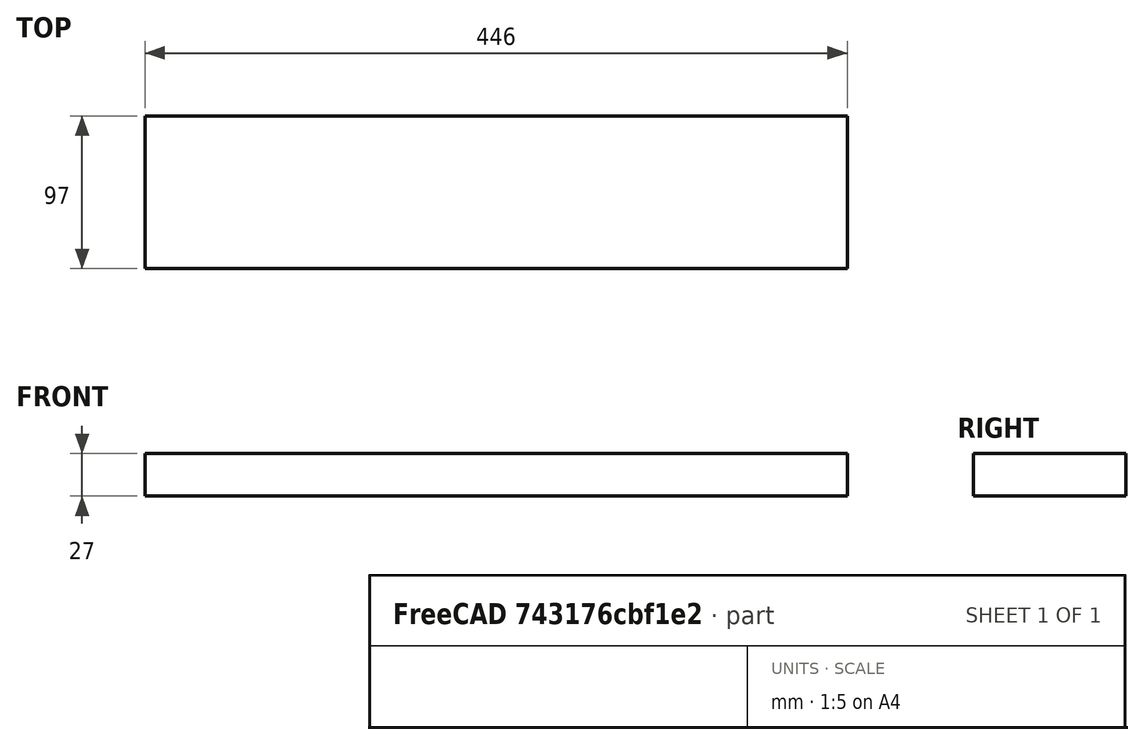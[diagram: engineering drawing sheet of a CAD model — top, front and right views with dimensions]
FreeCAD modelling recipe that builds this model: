
FCSTD DOCUMENT  (FreeCAD 0.20R25131 (Git))
Label: Innen_hinten
License: All rights reserved
LicenseURL: http://en.wikipedia.org/wiki/All_rights_reserved
objects: Part::FeaturePython×8, App::FeaturePython×2, Part::Box×1
note: 8 computed .brp shape members not serialized (recipe doc carries the construction recipe); baked Part::Feature solids carry a one-line shape summary decoded from their .brp
EXTERNAL_REF file=Grunddaten.FCStd obj=Spreadsheet

FEATURE [Part::Box] Box  label="Cube"
  AttacherType = Attacher::AttachEngine3D
  Height = 27
  Length = 446
  Width = 97
  expr: Length = <<Grunddaten>>#Spreadsheet.Innenmass
  expr: Width = <<Grunddaten>>#Spreadsheet.Hoehe
  expr: Height = <<Grunddaten>>#Spreadsheet.Plattendicke
FEATURE [App::FeaturePython] Constraints  # WARN: FeaturePython — macro-defined, semantics opaque (R4)
  _Version = 1
FEATURE [Part::FeaturePython] Parts  # WARN: FeaturePython — macro-defined, semantics opaque (R4)
  Group = -> [Box]
  GroupMode = 0
FEATURE [Part::FeaturePython] Assembly  label="Innen_hinten"  # WARN: FeaturePython — macro-defined, semantics opaque (R4)
  AutoRelax = true
  BuildShape = 0
  Freeze = false
  Group = -> [Constraints,Elements,Parts]
  Verbose = false
  _SolverType = 1
  _Version = 1
FEATURE [App::FeaturePython] Elements  # WARN: FeaturePython — macro-defined, semantics opaque (R4)
  Group = -> [Element,Element001,Element002,Element003,Element004,Element005]
FEATURE [Part::FeaturePython] Element  label="Oben"  # link proxy (typed FeaturePython)
  Detach = false
  LinkTransform = true
  LinkedObject = -> Box [Face4]
  _Parent = -> Elements
FEATURE [Part::FeaturePython] Element001  label="Hinten"  # link proxy (typed FeaturePython)
  Detach = false
  LinkTransform = true
  LinkedObject = -> Box [Face5]
  _Parent = -> Elements
FEATURE [Part::FeaturePython] Element002  # link proxy (typed FeaturePython)
  Detach = false
  LinkTransform = true
  LinkedObject = -> Box [Face1]
  _Parent = -> Elements
FEATURE [Part::FeaturePython] Element003  # link proxy (typed FeaturePython)
  Detach = false
  LinkTransform = true
  LinkedObject = -> Box [Face6]
  _Parent = -> Elements
FEATURE [Part::FeaturePython] Element004  # link proxy (typed FeaturePython)
  Detach = false
  LinkTransform = true
  LinkedObject = -> Box [Face2]
  _Parent = -> Elements
FEATURE [Part::FeaturePython] Element005  # link proxy (typed FeaturePython)
  Detach = false
  LinkTransform = true
  LinkedObject = -> Box [Face3]
  _Parent = -> Elements
